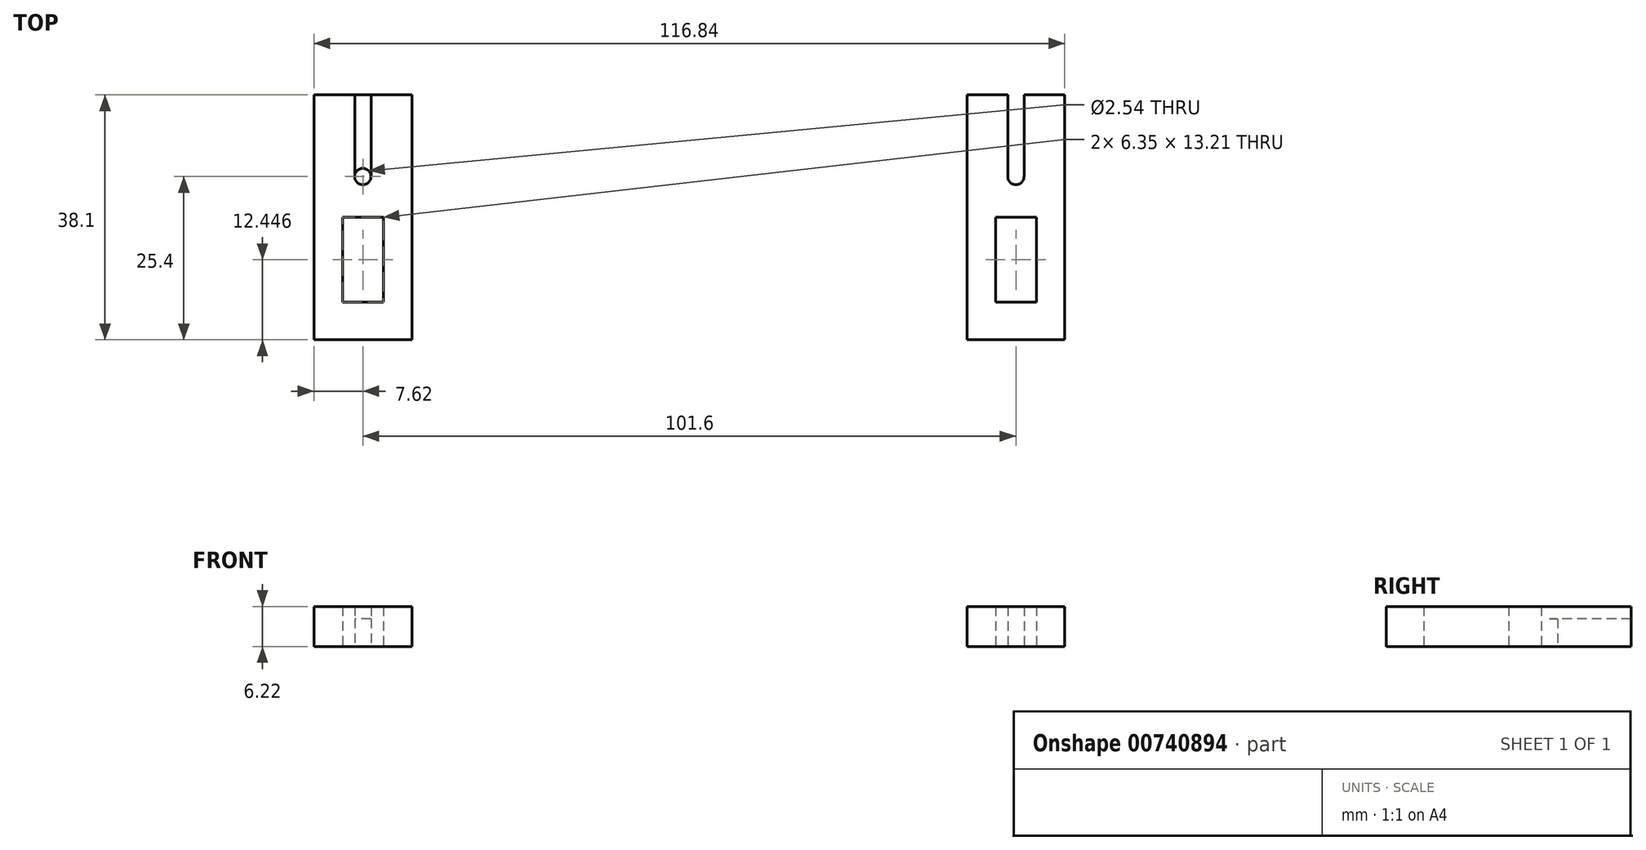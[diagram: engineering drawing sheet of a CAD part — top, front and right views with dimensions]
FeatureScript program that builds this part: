
annotation { "Feature Type Name" : "Feature", "Feature Type Description" : "" }
export const myFeature = defineFeature(function(context is Context, id is Id, definition is map)
    precondition{}
    {
        {
            var Q0;
            Q0=qCreatedBy(makeId("Top.planeOp"),FACE);
            var sketch = newSketch(context, id + "F0", { "sketchPlane" : qUnion([Q0])});
            skLineSegment(sketch, "E0.bottom", {"start": v(58.42, -25.4) * mm, "end": v(-58.42, -25.4) * mm});
            skLineSegment(sketch, "E0.top", {"start": v(58.42, 25.4) * mm, "end": v(-58.42, 25.4) * mm});
            skLineSegment(sketch, "E0.left", {"start": v(58.42, -25.4) * mm, "end": v(58.42, 25.4) * mm});
            skLineSegment(sketch, "E0.right", {"start": v(-58.42, -25.4) * mm, "end": v(-58.42, 25.4) * mm});
            skPoint(sketch, "E0.middle", {"position": v(0, 0) * mm});
            skLineSegment(sketch, "E1.bottom", {"start": v(-52.07, 25.4) * mm, "end": v(-49.53, 25.4) * mm});
            skLineSegment(sketch, "E1.top", {"start": v(-52.07, 12.7) * mm, "end": v(-49.53, 12.7) * mm});
            skLineSegment(sketch, "E1.left", {"start": v(-52.07, 25.4) * mm, "end": v(-52.07, 12.7) * mm});
            skLineSegment(sketch, "E1.right", {"start": v(-49.53, 25.4) * mm, "end": v(-49.53, 12.7) * mm});
            skCircle(sketch, "E2", {"center": v(-50.8, 12.7) * mm, "radius": 1.27 * mm});
            skLineSegment(sketch, "E3.MirrorCS", {"start": v(52.07, 25.4) * mm, "end": v(49.53, 25.4) * mm});
            skLineSegment(sketch, "E4.MirrorCS", {"start": v(49.53, 25.4) * mm, "end": v(49.53, 12.7) * mm});
            skLineSegment(sketch, "E5.MirrorCS", {"start": v(52.07, 25.4) * mm, "end": v(52.07, 12.7) * mm});
            skLineSegment(sketch, "E6.MirrorCS", {"start": v(52.07, 12.7) * mm, "end": v(49.53, 12.7) * mm});
            skCircle(sketch, "E7.MirrorC", {"center": v(50.8, 12.7) * mm, "radius": 1.27 * mm});
            skLineSegment(sketch, "E8.bottom", {"start": v(-47.63, -6.86) * mm, "end": v(-53.98, -6.86) * mm});
            skLineSegment(sketch, "E8.top", {"start": v(-47.63, 6.35) * mm, "end": v(-53.98, 6.35) * mm});
            skLineSegment(sketch, "E8.left", {"start": v(-47.63, -6.86) * mm, "end": v(-47.63, 6.35) * mm});
            skLineSegment(sketch, "E8.right", {"start": v(-53.98, -6.86) * mm, "end": v(-53.98, 6.35) * mm});
            skPoint(sketch, "E8.middle", {"position": v(-50.8, -0.25) * mm});
            skPoint(sketch, "E9.MirrorP", {"position": v(50.8, -0.25) * mm});
            skLineSegment(sketch, "E10.MirrorCS", {"start": v(47.63, 6.35) * mm, "end": v(53.98, 6.35) * mm});
            skLineSegment(sketch, "E11.MirrorCS", {"start": v(47.63, -6.86) * mm, "end": v(53.98, -6.86) * mm});
            skLineSegment(sketch, "E12.MirrorCS", {"start": v(53.98, -6.86) * mm, "end": v(53.98, 6.35) * mm});
            skLineSegment(sketch, "E13.MirrorCS", {"start": v(47.63, -6.86) * mm, "end": v(47.63, 6.35) * mm});
            skLineSegment(sketch, "E14.bottom", {"start": v(-58.42, 25.4) * mm, "end": v(-43.18, 25.4) * mm});
            skLineSegment(sketch, "E14.top", {"start": v(-58.42, -12.7) * mm, "end": v(-43.18, -12.7) * mm});
            skLineSegment(sketch, "E14.left", {"start": v(-58.42, 25.4) * mm, "end": v(-58.42, -12.7) * mm});
            skLineSegment(sketch, "E14.right", {"start": v(-43.18, 25.4) * mm, "end": v(-43.18, -12.7) * mm});
            skPoint(sketch, "E14.middle", {"position": v(-50.8, 6.35) * mm});
            skLineSegment(sketch, "E15.MirrorCS", {"start": v(58.42, -12.7) * mm, "end": v(43.18, -12.7) * mm});
            skLineSegment(sketch, "E16.MirrorCS", {"start": v(43.18, 25.4) * mm, "end": v(43.18, -12.7) * mm});
            skSolve(sketch);
        }
        {
            var Q0;
            {var subQ2=sQuery(id+"F0.wireOp",EDGE,"E4.MirrorCS");Q0=makeQuery(id+"F0.imprint","IMPRINT",FACE,{"disambiguationData":[TD([[makeQuery(id+"F0.imprint","IMPRINT",EDGE,{"derivedFrom":subQ2}),-1.0]])]});}
            var Q1;
            {var subQ3=sQuery(id+"F0.wireOp",EDGE,"E1.left");Q1=makeQuery(id+"F0.imprint","IMPRINT",FACE,{"disambiguationData":[TD([[makeQuery(id+"F0.imprint","IMPRINT",EDGE,{"derivedFrom":subQ3}),-1.0]])]});}
            extrude(context, id + "F1", {"entities" : qUnion([Q0, Q1]), "depth" : 6.22 * mm, "offsetDistance" : 25.4 * mm});
        }
        {
            var Q0;
            Q0=makeQuery(id+"F0.imprint","IMPRINT",FACE,{"disambiguationData":[TD([[makeQuery(id+"F0.imprint","IMPRINT",EDGE,{"derivedFrom":sQuery(id+"F0.wireOp",EDGE,"E3.MirrorCS")}),1.0]])]});
            var Q1;
            {var subQ0=sQuery(id+"F0.wireOp",EDGE,"E1.left");Q1=makeQuery(id+"F0.imprint","IMPRINT",FACE,{"disambiguationData":[TD([[makeQuery(id+"F0.imprint","IMPRINT",EDGE,{"derivedFrom":subQ0}),1.0]])]});}
            extrude(context, id + "F2", {"entities" : qUnion([Q0, Q1]), "operationType" : NewBodyOperationType.ADD, "depth" : 4.32 * mm, "offsetDistance" : 25.4 * mm});
        }
    });
